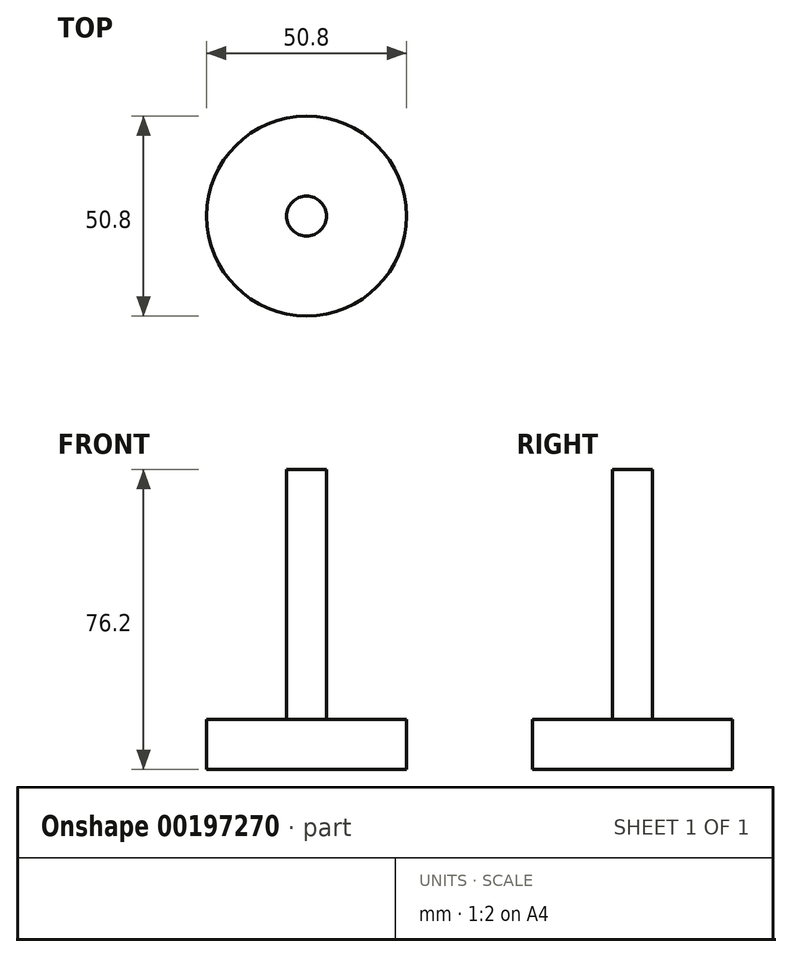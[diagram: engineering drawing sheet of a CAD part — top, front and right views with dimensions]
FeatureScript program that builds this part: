
annotation { "Feature Type Name" : "Feature", "Feature Type Description" : "" }
export const myFeature = defineFeature(function(context is Context, id is Id, definition is map)
    precondition{}
    {
        {
            var Q0;
            Q0=qCreatedBy(makeId("Top.planeOp"),FACE);
            var sketch = newSketch(context, id + "F0", { "sketchPlane" : qUnion([Q0])});
            skCircle(sketch, "E0", {"center": v(0, 0) * mm, "radius": 25.4 * mm});
            skSolve(sketch);
        }
        {
            var Q0;
            Q0=makeQuery(id+"F0.imprint","IMPRINT",FACE,{"disambiguationData":[TD([[makeQuery(id+"F0.imprint","IMPRINT",EDGE,{"derivedFrom":sQuery(id+"F0.wireOp",EDGE,"E0")}),1.0]])]});
            extrude(context, id + "F1", {"entities" : qUnion([Q0]), "depth" : 12.7 * mm});
        }
        {
            var Q0;
            Q0=qCreatedBy(makeId("Top.planeOp"),FACE);
            var sketch = newSketch(context, id + "F2", { "sketchPlane" : qUnion([Q0])});
            skCircle(sketch, "E1", {"center": v(0, 0) * mm, "radius": 5.08 * mm});
            skSolve(sketch);
        }
        {
            var Q0;
            Q0 = qSketchRegion(id + "F2", true);
            extrude(context, id + "F3", {"entities" : qUnion([Q0]), "operationType" : NewBodyOperationType.ADD, "depth" : 76.2 * mm});
        }
    });
